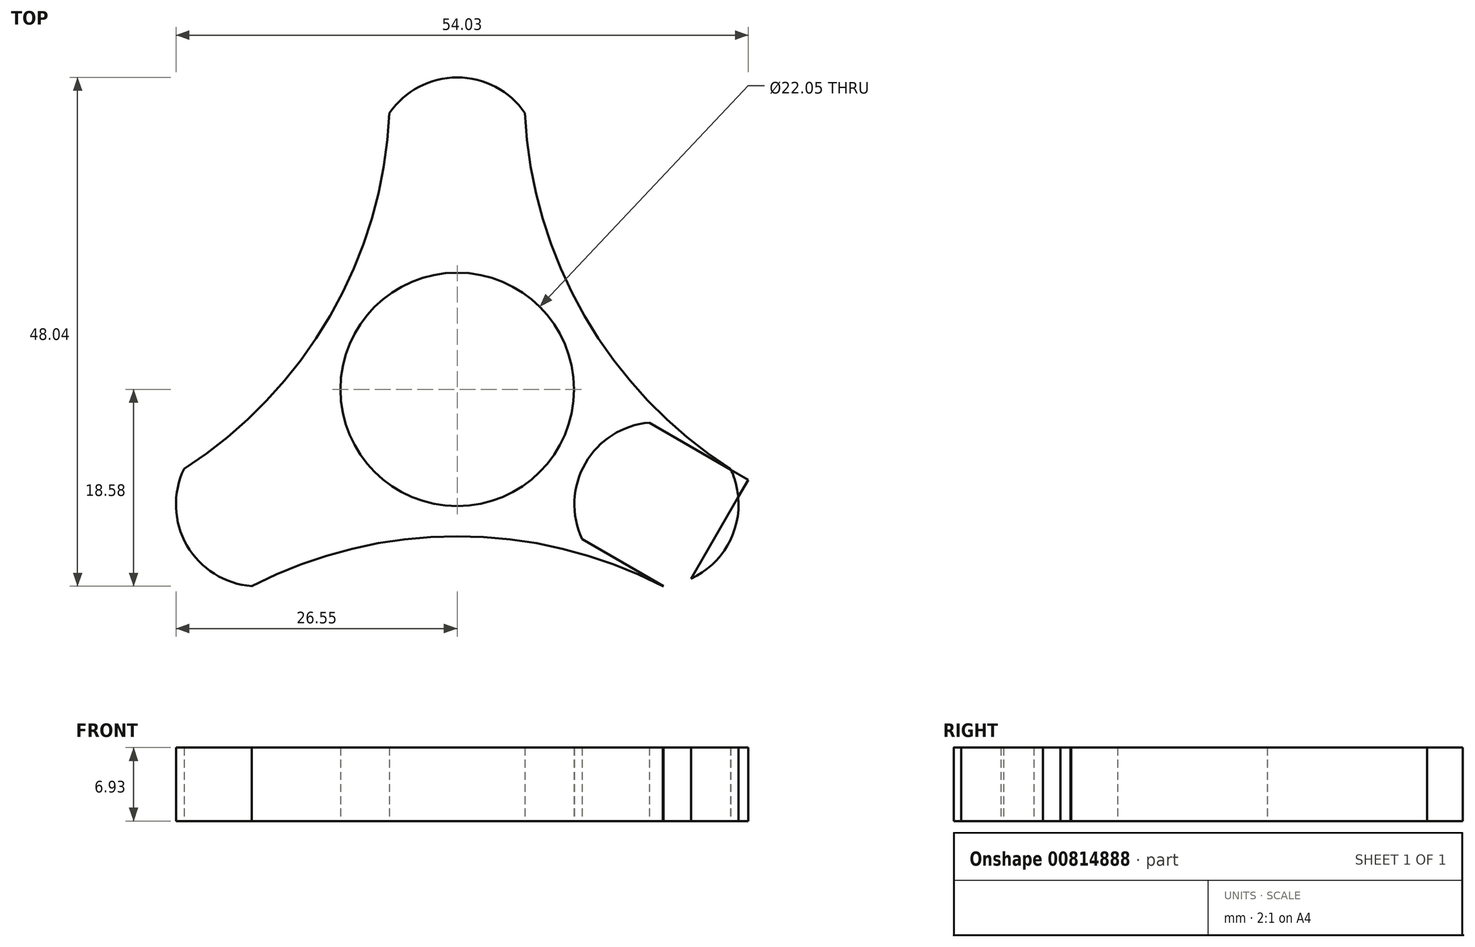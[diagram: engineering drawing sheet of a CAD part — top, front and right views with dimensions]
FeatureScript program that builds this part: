
annotation { "Feature Type Name" : "Feature", "Feature Type Description" : "" }
export const myFeature = defineFeature(function(context is Context, id is Id, definition is map)
    precondition{}
    {
        {
            var Q0;
            Q0=qCreatedBy(makeId("Top.planeOp"),FACE);
            var sketch = newSketch(context, id + "F0", { "sketchPlane" : qUnion([Q0])});
            skCircle(sketch, "E0", {"center": v(0, 0) * mm, "radius": 11.02 * mm});
            skLineSegment(sketch, "E1", {"start": v(0, 0) * mm, "end": v(0, 11.02) * mm});
            skLineSegment(sketch, "E2", {"start": v(0, 0) * mm, "end": v(9.55, -5.51) * mm});
            skLineSegment(sketch, "E3", {"start": v(0, 0) * mm, "end": v(-9.55, -5.51) * mm});
            skPoint(sketch, "E4", {"position": v(-6.35, 9.01) * mm});
            skPoint(sketch, "E5", {"position": v(6.35, 9.01) * mm});
            skPoint(sketch, "E6", {"position": v(10.98, 1) * mm});
            skPoint(sketch, "E7", {"position": v(4.63, -10) * mm});
            skLineSegment(sketch, "E8", {"start": v(6.35, 9.01) * mm, "end": v(-6.35, 9.01) * mm});
            skLineSegment(sketch, "E9", {"start": v(10.98, 1) * mm, "end": v(4.63, -10) * mm});
            skPoint(sketch, "E10", {"position": v(-4.63, -10) * mm});
            skPoint(sketch, "E11", {"position": v(-10.98, 1) * mm});
            skLineSegment(sketch, "E12", {"start": v(-10.98, 1) * mm, "end": v(-4.63, -10) * mm});
            skLineSegment(sketch, "E13", {"start": v(10.98, 1) * mm, "end": v(27.48, -8.53) * mm});
            skLineSegment(sketch, "E14", {"start": v(27.48, -8.53) * mm, "end": v(21.13, -19.53) * mm});
            skLineSegment(sketch, "E15", {"start": v(21.13, -19.53) * mm, "end": v(4.63, -10) * mm});
            skLineSegment(sketch, "E16", {"start": v(-4.63, -10) * mm, "end": v(-21.13, -19.53) * mm});
            skLineSegment(sketch, "E17", {"start": v(-21.13, -19.53) * mm, "end": v(-27.48, -8.53) * mm});
            skLineSegment(sketch, "E18", {"start": v(-27.48, -8.53) * mm, "end": v(-10.98, 1) * mm});
            skLineSegment(sketch, "E19", {"start": v(-6.35, 9.01) * mm, "end": v(-6.35, 28.06) * mm});
            skLineSegment(sketch, "E20", {"start": v(-6.35, 28.06) * mm, "end": v(6.35, 28.06) * mm});
            skLineSegment(sketch, "E21", {"start": v(6.35, 28.06) * mm, "end": v(6.35, 9.01) * mm});
            skArc(sketch, "E22", {"start": v(-27.48, -8.53) * mm, "mid": v(-12.01, 6.93) * mm, "end": v(-6.35, 28.06) * mm});
            skArc(sketch, "E23", {"start": v(6.35, 28.06) * mm, "mid": v(12.01, 6.93) * mm, "end": v(27.48, -8.53) * mm});
            skArc(sketch, "E24", {"start": v(21.13, -19.53) * mm, "mid": v(0, -13.87) * mm, "end": v(-21.13, -19.53) * mm});
            skPoint(sketch, "E25", {"position": v(0, 28.06) * mm});
            skPoint(sketch, "E26", {"position": v(24.3, -14.03) * mm});
            skPoint(sketch, "E27", {"position": v(-24.3, -14.03) * mm});
            skPoint(sketch, "E28", {"position": v(-26.52, -10.18) * mm});
            skPoint(sketch, "E29", {"position": v(-21.13, -19.53) * mm});
            skPoint(sketch, "E30", {"position": v(-22.08, -17.88) * mm});
            skPoint(sketch, "E31", {"position": v(22.08, -17.88) * mm});
            skPoint(sketch, "E32", {"position": v(26.52, -10.18) * mm});
            skPoint(sketch, "E33", {"position": v(4.45, 28.06) * mm});
            skPoint(sketch, "E34", {"position": v(-4.44, 28.06) * mm});
            skPoint(sketch, "E35", {"position": v(25.83, -7.58) * mm});
            skPoint(sketch, "E36", {"position": v(19.48, -18.58) * mm});
            skPoint(sketch, "E37", {"position": v(-12.88, -14.77) * mm});
            skPoint(sketch, "E38", {"position": v(-19.23, -3.77) * mm});
            skPoint(sketch, "E39", {"position": v(-6.35, 18.54) * mm});
            skPoint(sketch, "E40", {"position": v(6.35, 18.54) * mm});
            skPoint(sketch, "E41", {"position": v(-6.35, 26.16) * mm});
            skPoint(sketch, "E42", {"position": v(6.35, 26.16) * mm});
            skPoint(sketch, "E43", {"position": v(-19.48, -18.58) * mm});
            skPoint(sketch, "E44", {"position": v(-25.83, -7.58) * mm});
            skArc(sketch, "E45", {"start": v(-6.35, 26.16) * mm, "mid": v(5.48, 16.23) * mm, "end": v(-4.44, 28.06) * mm});
            skArc(sketch, "E46", {"start": v(25.83, -7.58) * mm, "mid": v(11.32, -12.86) * mm, "end": v(26.52, -10.18) * mm});
            skArc(sketch, "E47", {"start": v(-19.48, -18.58) * mm, "mid": v(-16.8, -3.37) * mm, "end": v(-22.08, -17.88) * mm});
            skArc(sketch, "E48", {"start": v(25.83, -7.58) * mm, "mid": v(26.29, -8.85) * mm, "end": v(26.52, -10.18) * mm});
            skArc(sketch, "E49", {"start": v(-22.08, -17.88) * mm, "mid": v(-20.8, -18.34) * mm, "end": v(-19.48, -18.58) * mm});
            skArc(sketch, "E50", {"start": v(-4.45, 28.06) * mm, "mid": v(-5.48, 27.2) * mm, "end": v(-6.35, 26.16) * mm});
            skSolve(sketch);
        }
        {
            var Q0;
            {var subQ4=sQuery(id+"F0.wireOp",EDGE,"E47");var subQ7=sQuery(id+"F0.wireOp",EDGE,"E16");var subQ9=makeQuery(id+"F0.imprint","INTERSECT",VERTEX,{"derivedFrom":[subQ7,subQ4]});Q0=makeQuery(id+"F0.imprint","IMPRINT",FACE,{"disambiguationData":[TD([[makeQuery(id+"F0.imprint","IMPRINT",EDGE,{"disambiguationData":[TD([[subQ9,-1.0]])],"derivedFrom":subQ4}),-1.0]])]});}
            var Q1;
            {var subQ0=sQuery(id+"F0.wireOp",EDGE,"E47");var subQ1=sQuery(id+"F0.wireOp",EDGE,"E22");var subQ2=makeQuery(id+"F0.imprint","INTERSECT",VERTEX,{"disambiguationData":[OD(1.0)],"derivedFrom":[subQ1,subQ0]});Q1=makeQuery(id+"F0.imprint","IMPRINT",FACE,{"disambiguationData":[TD([[makeQuery(id+"F0.imprint","IMPRINT",EDGE,{"disambiguationData":[TD([[subQ2,-1.0]])],"derivedFrom":subQ1}),-1.0]])]});}
            var Q2;
            {var subQ0=sQuery(id+"F0.wireOp",EDGE,"E19");var subQ4=sQuery(id+"F0.wireOp",EDGE,"E45");var subQ5=makeQuery(id+"F0.imprint","INTERSECT",VERTEX,{"derivedFrom":[subQ0,subQ4]});Q2=makeQuery(id+"F0.imprint","IMPRINT",FACE,{"disambiguationData":[TD([[makeQuery(id+"F0.imprint","IMPRINT",EDGE,{"disambiguationData":[TD([[subQ5,-1.0]])],"derivedFrom":subQ4}),-1.0]])]});}
            var Q3;
            {var subQ3=sQuery(id+"F0.wireOp",EDGE,"E45");var subQ9=sQuery(id+"F0.wireOp",EDGE,"E23");var subQ10=makeQuery(id+"F0.imprint","INTERSECT",VERTEX,{"disambiguationData":[OD(1.0)],"derivedFrom":[subQ9,subQ3]});Q3=makeQuery(id+"F0.imprint","IMPRINT",FACE,{"disambiguationData":[TD([[makeQuery(id+"F0.imprint","IMPRINT",EDGE,{"disambiguationData":[TD([[subQ10,-1.0]])],"derivedFrom":subQ9}),-1.0]])]});}
            var Q4;
            {var subQ4=sQuery(id+"F0.wireOp",EDGE,"E46");var subQ7=sQuery(id+"F0.wireOp",EDGE,"E13");var subQ9=makeQuery(id+"F0.imprint","INTERSECT",VERTEX,{"derivedFrom":[subQ7,subQ4]});Q4=makeQuery(id+"F0.imprint","IMPRINT",FACE,{"disambiguationData":[TD([[makeQuery(id+"F0.imprint","IMPRINT",EDGE,{"disambiguationData":[TD([[subQ9,-1.0]])],"derivedFrom":subQ4}),-1.0]])]});}
            var Q5;
            {var subQ0=sQuery(id+"F0.wireOp",EDGE,"E46");var subQ1=sQuery(id+"F0.wireOp",EDGE,"E24");var subQ2=makeQuery(id+"F0.imprint","INTERSECT",VERTEX,{"disambiguationData":[OD(1.0)],"derivedFrom":[subQ1,subQ0]});Q5=makeQuery(id+"F0.imprint","IMPRINT",FACE,{"disambiguationData":[TD([[makeQuery(id+"F0.imprint","IMPRINT",EDGE,{"disambiguationData":[TD([[subQ2,-1.0]])],"derivedFrom":subQ1}),-1.0]])]});}
            var Q6;
            {var subQ6=sQuery(id+"F0.wireOp",EDGE,"E48");Q6=makeQuery(id+"F0.imprint","IMPRINT",FACE,{"disambiguationData":[TD([[makeQuery(id+"F0.imprint","IMPRINT",EDGE,{"derivedFrom":subQ6}),-1.0]])]});}
            var Q7;
            {var subQ6=sQuery(id+"F0.wireOp",EDGE,"E50");Q7=makeQuery(id+"F0.imprint","IMPRINT",FACE,{"disambiguationData":[TD([[makeQuery(id+"F0.imprint","IMPRINT",EDGE,{"derivedFrom":subQ6}),1.0]])]});}
            var Q8;
            {var subQ6=sQuery(id+"F0.wireOp",EDGE,"E49");Q8=makeQuery(id+"F0.imprint","IMPRINT",FACE,{"disambiguationData":[TD([[makeQuery(id+"F0.imprint","IMPRINT",EDGE,{"derivedFrom":subQ6}),1.0]])]});}
            var Q9;
            {var subQ0=sQuery(id+"F0.wireOp",EDGE,"E47");var subQ1=sQuery(id+"F0.wireOp",EDGE,"E18");var subQ2=makeQuery(id+"F0.imprint","INTERSECT",VERTEX,{"disambiguationData":[OD(0.0)],"derivedFrom":[subQ1,subQ0]});Q9=makeQuery(id+"F0.imprint","IMPRINT",FACE,{"disambiguationData":[TD([[makeQuery(id+"F0.imprint","IMPRINT",EDGE,{"disambiguationData":[TD([[subQ2,-1.0]])],"derivedFrom":subQ1}),1.0]])]});}
            var Q10;
            {var subQ0=sQuery(id+"F0.wireOp",EDGE,"E47");var subQ4=sQuery(id+"F0.wireOp",EDGE,"E24");var subQ5=makeQuery(id+"F0.imprint","INTERSECT",VERTEX,{"disambiguationData":[OD(0.0)],"derivedFrom":[subQ4,subQ0]});Q10=makeQuery(id+"F0.imprint","IMPRINT",FACE,{"disambiguationData":[TD([[makeQuery(id+"F0.imprint","IMPRINT",EDGE,{"disambiguationData":[TD([[subQ5,-1.0]])],"derivedFrom":subQ4}),-1.0]])]});}
            var Q11;
            {var subQ0=sQuery(id+"F0.wireOp",EDGE,"E46");var subQ1=sQuery(id+"F0.wireOp",EDGE,"E15");var subQ2=makeQuery(id+"F0.imprint","INTERSECT",VERTEX,{"disambiguationData":[OD(0.0)],"derivedFrom":[subQ1,subQ0]});Q11=makeQuery(id+"F0.imprint","IMPRINT",FACE,{"disambiguationData":[TD([[makeQuery(id+"F0.imprint","IMPRINT",EDGE,{"disambiguationData":[TD([[subQ2,-1.0]])],"derivedFrom":subQ1}),1.0]])]});}
            var Q12;
            {var subQ0=sQuery(id+"F0.wireOp",EDGE,"E46");var subQ4=sQuery(id+"F0.wireOp",EDGE,"E23");var subQ6=makeQuery(id+"F0.imprint","INTERSECT",VERTEX,{"disambiguationData":[OD(0.0)],"derivedFrom":[subQ4,subQ0]});Q12=makeQuery(id+"F0.imprint","IMPRINT",FACE,{"disambiguationData":[TD([[makeQuery(id+"F0.imprint","IMPRINT",EDGE,{"disambiguationData":[TD([[subQ6,-1.0]])],"derivedFrom":subQ4}),-1.0]])]});}
            var Q13;
            {var subQ0=sQuery(id+"F0.wireOp",EDGE,"E45");var subQ1=sQuery(id+"F0.wireOp",EDGE,"E21");var subQ2=makeQuery(id+"F0.imprint","INTERSECT",VERTEX,{"disambiguationData":[OD(0.0)],"derivedFrom":[subQ1,subQ0]});Q13=makeQuery(id+"F0.imprint","IMPRINT",FACE,{"disambiguationData":[TD([[makeQuery(id+"F0.imprint","IMPRINT",EDGE,{"disambiguationData":[TD([[subQ2,-1.0]])],"derivedFrom":subQ1}),1.0]])]});}
            var Q14;
            {var subQ0=sQuery(id+"F0.wireOp",EDGE,"E45");var subQ4=sQuery(id+"F0.wireOp",EDGE,"E22");var subQ5=makeQuery(id+"F0.imprint","INTERSECT",VERTEX,{"disambiguationData":[OD(0.0)],"derivedFrom":[subQ4,subQ0]});Q14=makeQuery(id+"F0.imprint","IMPRINT",FACE,{"disambiguationData":[TD([[makeQuery(id+"F0.imprint","IMPRINT",EDGE,{"disambiguationData":[TD([[subQ5,-1.0]])],"derivedFrom":subQ4}),-1.0]])]});}
            var Q15;
            {var subQ0=sQuery(id+"F0.wireOp",EDGE,"E47");var subQ1=sQuery(id+"F0.wireOp",EDGE,"E17");var subQ3=makeQuery(id+"F0.imprint","INTERSECT",VERTEX,{"derivedFrom":[subQ1,subQ0]});Q15=makeQuery(id+"F0.imprint","IMPRINT",FACE,{"disambiguationData":[TD([[makeQuery(id+"F0.imprint","IMPRINT",EDGE,{"disambiguationData":[TD([[subQ3,1.0]])],"derivedFrom":subQ1}),1.0]])]});}
            var Q16;
            {var subQ0=sQuery(id+"F0.wireOp",EDGE,"E46");var subQ1=sQuery(id+"F0.wireOp",EDGE,"E14");var subQ3=makeQuery(id+"F0.imprint","INTERSECT",VERTEX,{"derivedFrom":[subQ1,subQ0]});Q16=makeQuery(id+"F0.imprint","IMPRINT",FACE,{"disambiguationData":[TD([[makeQuery(id+"F0.imprint","IMPRINT",EDGE,{"disambiguationData":[TD([[subQ3,1.0]])],"derivedFrom":subQ1}),1.0]])]});}
            var Q17;
            {var subQ0=sQuery(id+"F0.wireOp",EDGE,"E45");var subQ1=sQuery(id+"F0.wireOp",EDGE,"E20");var subQ3=makeQuery(id+"F0.imprint","INTERSECT",VERTEX,{"derivedFrom":[subQ1,subQ0]});Q17=makeQuery(id+"F0.imprint","IMPRINT",FACE,{"disambiguationData":[TD([[makeQuery(id+"F0.imprint","IMPRINT",EDGE,{"disambiguationData":[TD([[subQ3,1.0]])],"derivedFrom":subQ1}),1.0]])]});}
            extrude(context, id + "F1", {"entities" : qUnion([Q0, Q1, Q2, Q3, Q4, Q5, Q6, Q7, Q8, Q9, Q10, Q11, Q12, Q13, Q14, Q15, Q16, Q17]), "depth" : 6.93 * mm, "offsetDistance" : 25.4 * mm});
        }
    });
